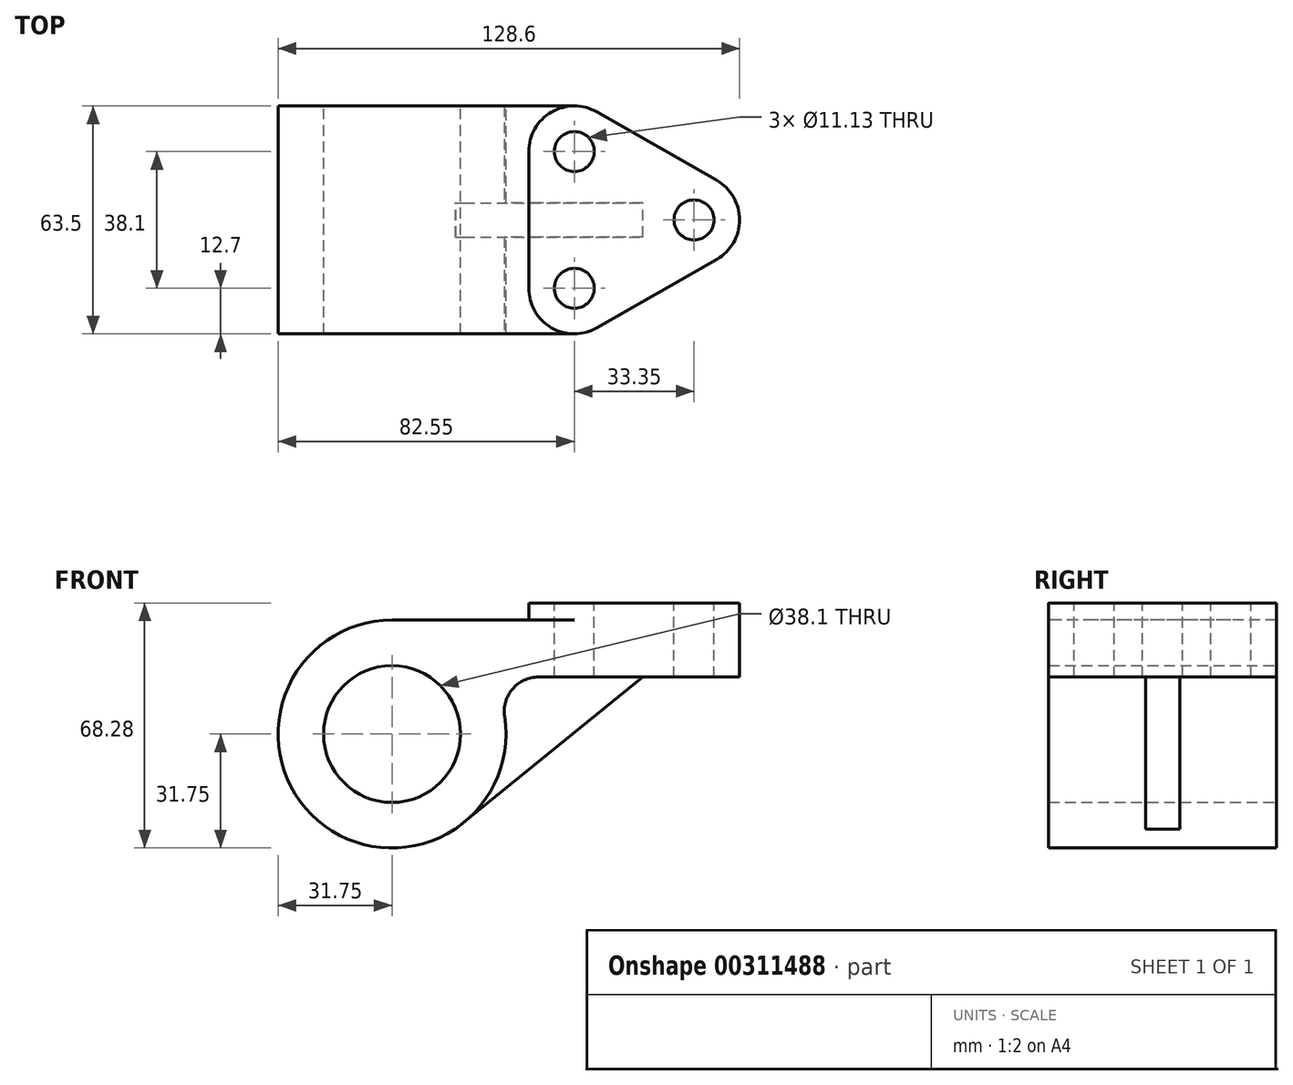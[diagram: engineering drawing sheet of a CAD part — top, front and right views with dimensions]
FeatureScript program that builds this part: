
annotation { "Feature Type Name" : "Feature", "Feature Type Description" : "" }
export const myFeature = defineFeature(function(context is Context, id is Id, definition is map)
    precondition{}
    {
        {
            var Q0;
            Q0=qCreatedBy(makeId("Front.planeOp"),FACE);
            var sketch = newSketch(context, id + "F0", { "sketchPlane" : qUnion([Q0])});
            skCircle(sketch, "E0", {"center": v(0, 0) * mm, "radius": 31.75 * mm});
            skCircle(sketch, "E1", {"center": v(0, 0) * mm, "radius": 19.05 * mm});
            skSolve(sketch);
        }
        {
            var Q0;
            Q0 = qSketchRegion(id + "F0", true);
            extrude(context, id + "F1", {"entities" : qUnion([Q0]), "depth" : 63.5 * mm});
        }
        {
            var Q0;
            Q0=qCreatedBy(makeId("Top.planeOp"),FACE);
            cPlane(context, id + "F2", {"entities" : qUnion([Q0]), "cplaneType" : CPlaneType.OFFSET, "offset" : 31.75 * mm, "width" : 152.4 * mm, "height" : 152.4 * mm});
        }
        {
            var Q0;
            Q0=qCreatedBy(id+"F2.planeOp",FACE);
            var sketch = newSketch(context, id + "F3", { "sketchPlane" : qUnion([Q0])});
            skLineSegment(sketch, "E2", {"start": v(0, 0) * mm, "end": v(50.8, 0) * mm});
            skLineSegment(sketch, "E3", {"start": v(0, -63.5) * mm, "end": v(50.8, -63.5) * mm});
            skArc(sketch, "E4", {"start": v(57.1, -1.67) * mm, "mid": v(54.06, -0.43) * mm, "end": v(50.8, 0) * mm});
            skArc(sketch, "E5", {"start": v(50.8, -63.5) * mm, "mid": v(54.06, -63.07) * mm, "end": v(57.1, -61.83) * mm});
            skArc(sketch, "E6", {"start": v(90.45, -42.78) * mm, "mid": v(96.85, -31.75) * mm, "end": v(90.45, -20.72) * mm});
            skLineSegment(sketch, "E7", {"start": v(90.45, -20.72) * mm, "end": v(57.1, -1.67) * mm});
            skLineSegment(sketch, "E8", {"start": v(57.1, -61.83) * mm, "end": v(90.45, -42.78) * mm});
            skLineSegment(sketch, "E9", {"start": v(50.8, -12.7) * mm, "end": v(84.15, -31.75) * mm, "construction": true});
            skLineSegment(sketch, "E10", {"start": v(50.8, -50.8) * mm, "end": v(84.15, -31.75) * mm, "construction": true});
            skLineSegment(sketch, "E11", {"start": v(50.8, -50.8) * mm, "end": v(50.8, -12.7) * mm, "construction": true});
            skLineSegment(sketch, "E12", {"start": v(50.8, 0) * mm, "end": v(50.8, -12.7) * mm, "construction": true});
            skLineSegment(sketch, "E13", {"start": v(50.8, -50.8) * mm, "end": v(50.8, -63.5) * mm, "construction": true});
            skLineSegment(sketch, "E14", {"start": v(0, 0) * mm, "end": v(0, -63.5) * mm});
            skSolve(sketch);
        }
        {
            var Q0;
            Q0 = qSketchRegion(id + "F3", true);
            extrude(context, id + "F4", {"entities" : qUnion([Q0]), "operationType" : NewBodyOperationType.ADD, "oppositeDirection" : true, "depth" : 15.88 * mm});
        }
        {
            var Q0;
            Q0=makeQuery(id+"F0.imprint","IMPRINT",FACE,{"disambiguationData":[TD([[makeQuery(id+"F0.imprint","IMPRINT",EDGE,{"derivedFrom":sQuery(id+"F0.wireOp",EDGE,"E1")}),1.0]])]});
            extrude(context, id + "F5", {"entities" : qUnion([Q0]), "operationType" : NewBodyOperationType.REMOVE, "endBound" : BoundingType.THROUGH_ALL, "depth" : 25.4 * mm});
        }
        {
            var Q0;
            Q0=makeQuery(id+"F4.boolean.opBoolean","MERGE",FACE,{"derivedFrom":[makeQuery(id+"F1.opExtrude","CAP_FACE",FACE,{"disambiguationData":[OSD([sQuery(id+"F0.wireOp",EDGE,"E0"),sQuery(id+"F0.wireOp",EDGE,"E1")])],"isStart":false}),makeQuery(id+"F4.opExtrude","SWEPT_FACE",FACE,{"disambiguationData":[OSD([sQuery(id+"F3.wireOp",EDGE,"E3")])]})]});
            var sketch = newSketch(context, id + "F6", { "sketchPlane" : qUnion([Q0])});
            skArc(sketch, "E15", {"start": v(40.78, 15.88) * mm, "mid": v(33.55, 12.55) * mm, "end": v(31.37, 4.88) * mm});
            skLineSegment(sketch, "E16", {"start": v(40.78, 15.88) * mm, "end": v(27.5, 15.88) * mm});
            skLineSegment(sketch, "E17", {"start": v(27.5, 15.88) * mm, "end": v(31.37, 4.88) * mm});
            skSolve(sketch);
        }
        {
            var Q0;
            Q0 = qSketchRegion(id + "F6", true);
            extrude(context, id + "F7", {"entities" : qUnion([Q0]), "operationType" : NewBodyOperationType.ADD, "oppositeDirection" : true, "depth" : 63.5 * mm});
        }
        {
            var Q0;
            Q0=makeQuery(id+"F4.opExtrude","CAP_FACE",FACE,{"disambiguationData":[OSD([sQuery(id+"F3.wireOp",EDGE,"E2"),sQuery(id+"F3.wireOp",EDGE,"E3"),sQuery(id+"F3.wireOp",EDGE,"E4"),sQuery(id+"F3.wireOp",EDGE,"E5"),sQuery(id+"F3.wireOp",EDGE,"E6"),sQuery(id+"F3.wireOp",EDGE,"E7"),sQuery(id+"F3.wireOp",EDGE,"E8"),sQuery(id+"F3.wireOp",EDGE,"E14")])],"isStart":true});
            var sketch = newSketch(context, id + "F8", { "sketchPlane" : qUnion([Q0])});
            skLineSegment(sketch, "E18", {"start": v(38.1, -12.7) * mm, "end": v(38.1, -50.8) * mm});
            skLineSegment(sketch, "E19", {"start": v(57.1, -61.83) * mm, "end": v(90.45, -42.78) * mm});
            skLineSegment(sketch, "E20", {"start": v(90.45, -20.72) * mm, "end": v(57.1, -1.67) * mm});
            skArc(sketch, "E21", {"start": v(90.45, -42.78) * mm, "mid": v(96.85, -31.75) * mm, "end": v(90.45, -20.72) * mm});
            skArc(sketch, "E22", {"start": v(38.1, -50.8) * mm, "mid": v(44.42, -61.78) * mm, "end": v(57.1, -61.83) * mm});
            skArc(sketch, "E23", {"start": v(57.1, -1.67) * mm, "mid": v(44.42, -1.72) * mm, "end": v(38.1, -12.7) * mm});
            skSolve(sketch);
        }
        {
            var Q0;
            Q0 = qSketchRegion(id + "F8", true);
            extrude(context, id + "F9", {"entities" : qUnion([Q0]), "operationType" : NewBodyOperationType.ADD, "depth" : 4.78 * mm});
        }
        {
            var Q0;
            Q0=makeQuery(id+"F9.opExtrude","CAP_FACE",FACE,{"disambiguationData":[OSD([sQuery(id+"F8.wireOp",EDGE,"E18"),sQuery(id+"F8.wireOp",EDGE,"E19"),sQuery(id+"F8.wireOp",EDGE,"E20"),sQuery(id+"F8.wireOp",EDGE,"E21"),sQuery(id+"F8.wireOp",EDGE,"E22"),sQuery(id+"F8.wireOp",EDGE,"E23")])],"isStart":false});
            var sketch = newSketch(context, id + "F10", { "sketchPlane" : qUnion([Q0])});
            skCircle(sketch, "E24", {"center": v(50.8, -12.7) * mm, "radius": 5.56 * mm});
            skCircle(sketch, "E25", {"center": v(50.8, -50.8) * mm, "radius": 5.56 * mm});
            skCircle(sketch, "E26", {"center": v(84.15, -31.75) * mm, "radius": 5.56 * mm});
            skSolve(sketch);
        }
        {
            var Q0;
            Q0 = qSketchRegion(id + "F10", true);
            extrude(context, id + "F11", {"entities" : qUnion([Q0]), "operationType" : NewBodyOperationType.REMOVE, "oppositeDirection" : true, "depth" : 25.4 * mm});
        }
        {
            var Q0;
            Q0=qCreatedBy(makeId("Front.planeOp"),FACE);
            cPlane(context, id + "F12", {"entities" : qUnion([Q0]), "cplaneType" : CPlaneType.OFFSET, "offset" : 31.75 * mm, "width" : 152.4 * mm, "height" : 152.4 * mm});
        }
        {
            var Q0;
            Q0=qCreatedBy(id+"F12.planeOp",FACE);
            var sketch = newSketch(context, id + "F13", { "sketchPlane" : qUnion([Q0])});
            skLineSegment(sketch, "E27", {"start": v(17.76, -26.48) * mm, "end": v(69.85, 15.88) * mm});
            skLineSegment(sketch, "E28", {"start": v(69.85, 15.88) * mm, "end": v(30.92, 15.88) * mm});
            skLineSegment(sketch, "E29", {"start": v(30.92, 15.88) * mm, "end": v(17.76, -26.48) * mm});
            skSolve(sketch);
        }
        {
            var Q0;
            Q0 = qSketchRegion(id + "F13", true);
            extrude(context, id + "F14", {"entities" : qUnion([Q0]), "operationType" : NewBodyOperationType.ADD, "endBound" : BoundingType.SYMMETRIC, "depth" : 9.52 * mm});
        }
    });
